# Revit family: Backflow_Preventer-DC-Zurn_Wilkins-Model_450_450G-(8-10_Inch)
name_source: partatom
category: Pipe Accessories
units: mm (PartAtom-declared; Revit-internal decimal feet)

## family parameters
Always vertical = Yes
Cut with Voids When Loaded = No
OmniClass Number = 23.65.55.14.21
OmniClass Title = Non-Return Valves for Liquid Services
Part Type = Valve - Breaks Into
Round Connector Dimension = Use Radius
Shared = No
Work Plane-Based = No

## types (4) — shared parameters
Assembly Code = D2020300
Bend Radius = 1"
Bend Radius Outside = 2"
DIM A - Inlet center to outlet center = 29"
DIM D - Center to cover coupling end = 8 31/32"
Default Elevation = 0"
Description = Double Check Valve Assembly
Flow Rate (GPM) = 0 GPM
Hydrostatic Test Pressure = 350.00 psi
Length = 29"
Main Material = Paint - Zurn - Blue - Ductile Iron
Manufacturer = Zurn Water, LLC
Manufacturer Brand = Zurn Wilkins
Max Working Water Pressure = 175.00 psi
Max Working Water Temperature = 140 °F
Modified Date = 10/22/2025
Overall Length = 29"
Pipe Size = 1 3/32"
Product Documentation Link = https://files.zurn.com
Product Installation Sheet URL = https://files.zurn.com
Product Page URL = https://www.zurn.com
Product data URL = https://www.bimobject.com
Repair Parts URL = https://files.zurn.com
URL = https://www.zurn.com

## per-type parameters (varying)
| type | DIM B - Overall height of the valve | DIM C - Center to gate valve stem top | Height | Main Body DA | Model | Nominal Diameter | Nominal Radius | Overall Height | Pressure Loss at Rated Flow | Product Weight (lbs) | Rated Flow | Shut Off Valve |
| 10-450G (10" 450G) | 47 1/2" | 24 3/4" | 47 1/2" | Main Body 450(8-10) : 10" | 450G | 10" | 5" | 47 1/2" | 6.00 psi | 980 | 2400 GPM | Gate Valve_450 NRS(8-10) : 10" G |
| 8-450G (8" 450G) | 46" | 21 1/8" | 46" | Main Body 450(8-10) : 8" | 450G | 8" | 4" | 46" | 3.50 psi | 798 | 1600 GPM | Gate Valve_450 NRS(8-10) : 8" G |
| 10-450 (10" 450) | 47 1/2" | 24 3/4" | 47 1/2" | Main Body 450(8-10) : 10" | 450 | 10" | 5" | 47 1/2" | 6.00 psi | 1032 | 2400 GPM | Gate Valve_450 NRS(8-10) : 10" |
| 8-450 (8" 450) | 46" | 21 1/8" | 46" | Main Body 450(8-10) : 8" | 450 | 8" | 4" | 46" | 3.50 psi | 838 | 1600 GPM | Gate Valve_450 NRS(8-10) : 8" |

## geometry (parser evidence)
native form markers: Sweep x11
no freeform markers — native parametric forms only
